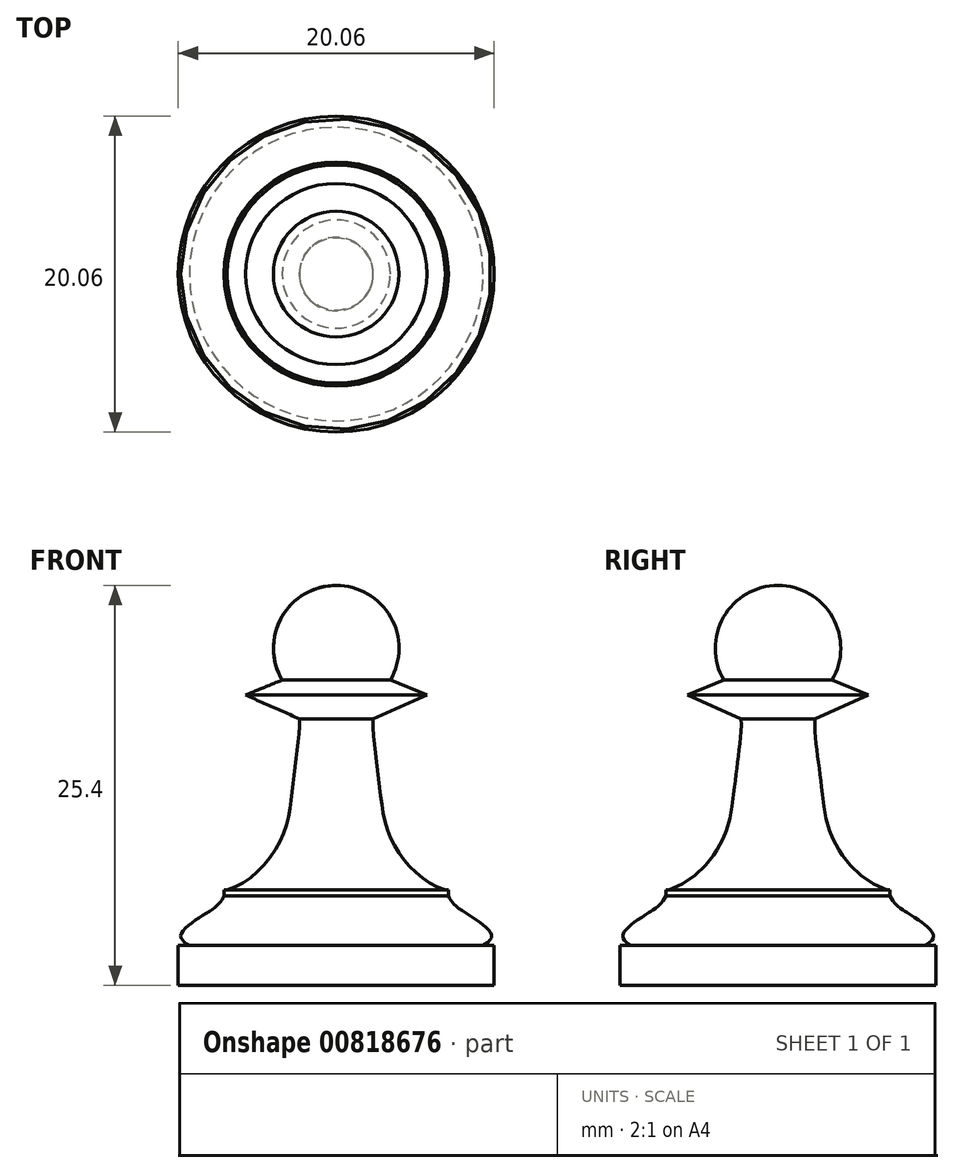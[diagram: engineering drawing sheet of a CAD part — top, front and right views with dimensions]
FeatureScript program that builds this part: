
annotation { "Feature Type Name" : "Feature", "Feature Type Description" : "" }
export const myFeature = defineFeature(function(context is Context, id is Id, definition is map)
    precondition{}
    {
        {
            var Q0;
            Q0=qCreatedBy(makeId("Front.planeOp"),FACE);
            var sketch = newSketch(context, id + "F0", { "sketchPlane" : qUnion([Q0])});
            skLineSegment(sketch, "E0", {"start": v(0, 0) * mm, "end": v(10.03, 0) * mm});
            skLineSegment(sketch, "E1", {"start": v(0, 0) * mm, "end": v(0, -25.4) * mm, "construction": true});
            skLineSegment(sketch, "E2", {"start": v(10.03, 0) * mm, "end": v(10.03, -2.53) * mm});
            skLineSegment(sketch, "E3", {"start": v(10.03, -2.53) * mm, "end": v(9.33, -2.53) * mm});
            skFitSpline(sketch, "E4", {"points": [v(9.33, -2.53) * mm, v(9.87, -3.14) * mm, v(8.72, -4.29) * mm, v(7.48, -5.14) * mm, v(7.12, -5.68) * mm], "startDerivative": vector(3.9, -2.6) * mm, "endDerivative": vector(-1.49, -2.82) * mm});
            skLineSegment(sketch, "E5", {"start": v(7.12, -5.68) * mm, "end": v(7.12, -6.07) * mm});
            skLineSegment(sketch, "E6", {"start": v(7.12, -6.07) * mm, "end": v(6.93, -6.07) * mm});
            skCircle(sketch, "E7", {"center": v(0, -21.41) * mm, "radius": 3.99 * mm});
            skLineSegment(sketch, "E8", {"start": v(0, -25.4) * mm, "end": v(0, 0) * mm});
            skLineSegment(sketch, "E9", {"start": v(5.76, -18.44) * mm, "end": v(3.44, -19.4) * mm});
            skFitSpline(sketch, "E10", {"points": [v(6.93, -6.07) * mm, v(3.55, -9.19) * mm, v(2.7, -13.18) * mm, v(2.34, -16.93) * mm], "startDerivative": vector(-11.76, -3.07) * mm, "endDerivative": vector(0.32, -10.83) * mm});
            skLineSegment(sketch, "E11", {"start": v(5.76, -18.44) * mm, "end": v(2.34, -16.93) * mm});
            skSolve(sketch);
        }
        {
            var Q0;
            {var subQ4=sQuery(id+"F0.wireOp",EDGE,"E0");Q0=makeQuery(id+"F0.imprint","IMPRINT",FACE,{"disambiguationData":[TD([[makeQuery(id+"F0.imprint","IMPRINT",EDGE,{"derivedFrom":subQ4}),-1.0]])]});}
            var Q1;
            {var subQ0=sQuery(id+"F0.wireOp",EDGE,"E7");var subQ1=makeQuery(id+"F0.imprint","INTERSECT",VERTEX,{"derivedFrom":[subQ0,sQuery(id+"F0.wireOp",EDGE,"b816689f-9f3e-4efa-b548-93b4ac524903")]});Q1=makeQuery(id+"F0.imprint","IMPRINT",FACE,{"disambiguationData":[TD([[makeQuery(id+"F0.imprint","IMPRINT",EDGE,{"disambiguationData":[TD([[subQ1,-1.0]])],"derivedFrom":subQ0}),1.0]])]});}
            var Q2;
            Q2=sQuery(id+"F0.wireOp",EDGE,"E8");
            revolve(context, id + "F1", {"surfaceOperationType" : NewSurfaceOperationType.NEW, "entities" : qUnion([Q0, Q1]), "axis" : qUnion([Q2]), "revolveType" : RevolveType.FULL});
        }
        {
            var Q0;
            Q0=makeQuery(id+"F1.opRevolve","SWEPT_BODY",BODY,{"disambiguationData":[OSD([sQuery(id+"F0.wireOp",EDGE,"E0"),sQuery(id+"F0.wireOp",EDGE,"E2"),sQuery(id+"F0.wireOp",EDGE,"E3"),sQuery(id+"F0.wireOp",EDGE,"E4"),sQuery(id+"F0.wireOp",EDGE,"E5"),sQuery(id+"F0.wireOp",EDGE,"E6"),sQuery(id+"F0.wireOp",EDGE,"E7"),sQuery(id+"F0.wireOp",EDGE,"E8"),sQuery(id+"F0.wireOp",EDGE,"E9"),sQuery(id+"F0.wireOp",EDGE,"E10"),sQuery(id+"F0.wireOp",EDGE,"E11")])]});
            var Q1;
            Q1=sQuery(id+"F0.wireOp",EDGE,"E0");
            transform(context, id + "F2", {"entities" : qUnion([Q0]), "transformType" : TransformType.ROTATION, "transformAxis" : qUnion([Q1]), "angle" : 180 * degree, "makeCopy" : false});
        }
    });
